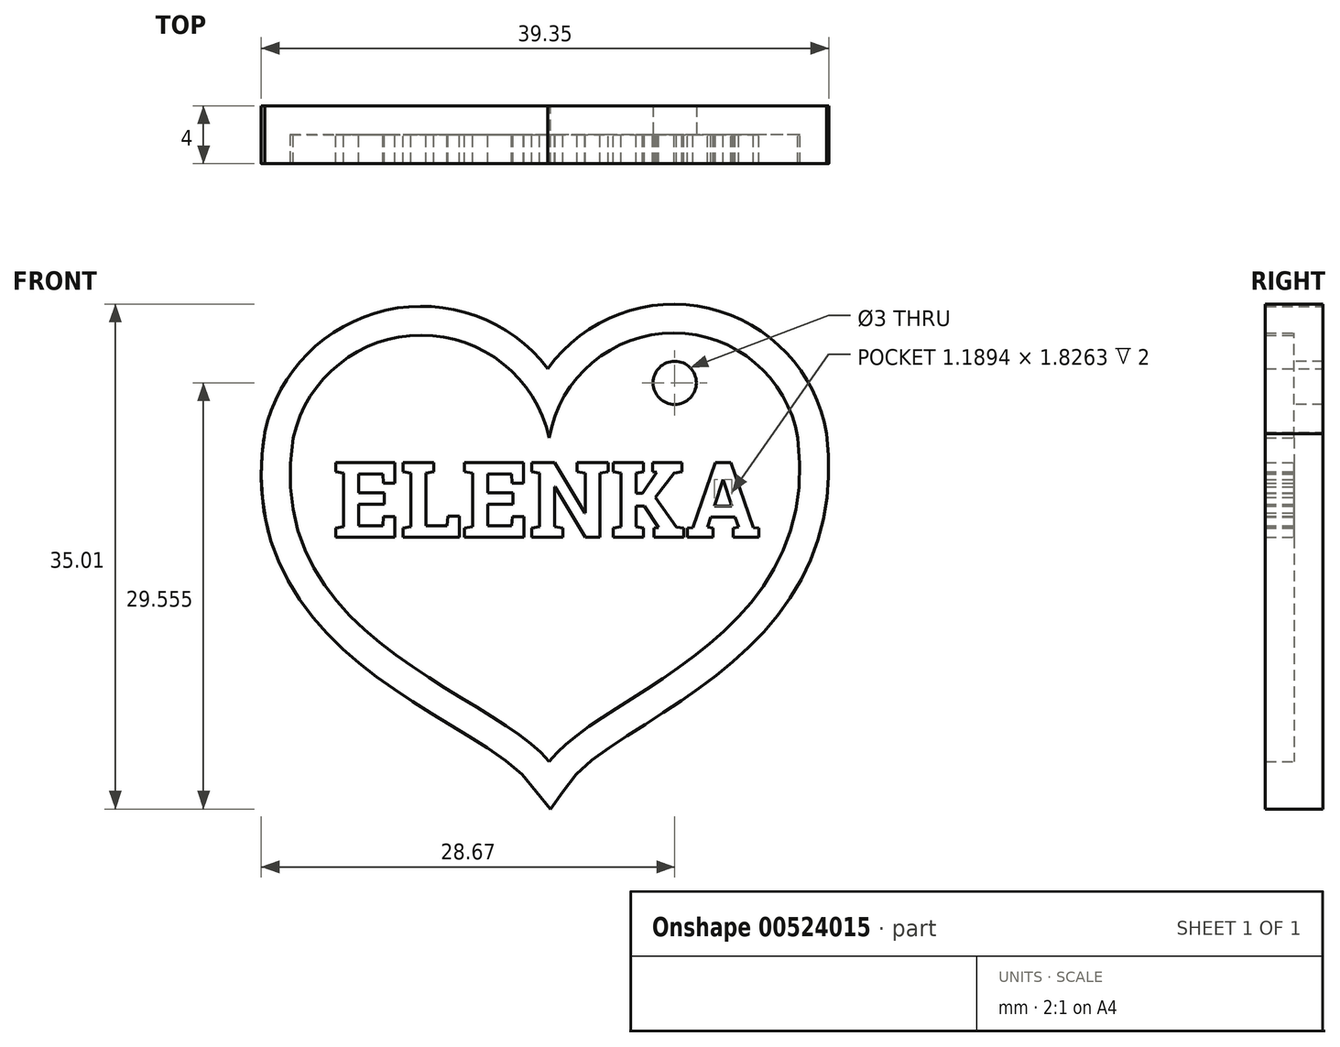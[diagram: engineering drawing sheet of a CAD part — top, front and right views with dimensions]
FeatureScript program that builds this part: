
annotation { "Feature Type Name" : "Feature", "Feature Type Description" : "" }
export const myFeature = defineFeature(function(context is Context, id is Id, definition is map)
    precondition{}
    {
        {
            var Q0;
            Q0=qCreatedBy(makeId("Front.planeOp"),FACE);
            var sketch = newSketch(context, id + "F0", { "sketchPlane" : qUnion([Q0])});
            skArc(sketch, "E0", {"start": v(17.25, 0) * mm, "mid": v(8.62, 7.26) * mm, "end": v(0, 0) * mm});
            skArc(sketch, "E1", {"start": v(0, 0) * mm, "mid": v(-8.88, 7.12) * mm, "end": v(-17.75, 0) * mm});
            skFitSpline(sketch, "E2", {"points": [v(-17.75, 0) * mm, v(0, -22.47) * mm], "startDerivative": vector(-6.74, -42.05) * mm, "endDerivative": vector(11.85, -14.75) * mm});
            skFitSpline(sketch, "E3", {"points": [v(17.25, 0) * mm, v(0, -22.47) * mm], "startDerivative": vector(5.09, -42.28) * mm, "endDerivative": vector(-10.5, -14.29) * mm});
            skSolve(sketch);
        }
        {
            var Q0;
            Q0=makeQuery(id+"F0.imprint","IMPRINT",FACE,{"disambiguationData":[TD([[makeQuery(id+"F0.imprint","IMPRINT",EDGE,{"derivedFrom":sQuery(id+"F0.wireOp",EDGE,"E0")}),1.0]])]});
            extrude(context, id + "F1", {"entities" : qUnion([Q0]), "depth" : 2 * mm, "offsetDistance" : 25 * mm});
        }
        {
            var Q0;
            Q0=makeQuery(id+"F1.opExtrude","CAP_FACE",FACE,{"disambiguationData":[OSD([sQuery(id+"F0.wireOp",EDGE,"E0"),sQuery(id+"F0.wireOp",EDGE,"E1"),sQuery(id+"F0.wireOp",EDGE,"E2"),sQuery(id+"F0.wireOp",EDGE,"E3")])],"isStart":false});
            shell(context, id + "F2", {"entities" : qUnion([Q0]), "thickness" : 2 * mm, "oppositeDirection" : true});
        }
        {
            var Q0;
            Q0=qCreatedBy(makeId("Front.planeOp"),FACE);
            var sketch = newSketch(context, id + "F3", { "sketchPlane" : qUnion([Q0])});
            skText(sketch, "E4", { "text": "ELENKA\n", "fontName": "RobotoSlab-Bold.ttf"});
            const initialGuessF3  = {"E4": [-0.015, -0.0069, 1, 0, 0.00525]};
            skSetInitialGuess(sketch, initialGuessF3);
            skSolve(sketch);
        }
        {
            var Q0;
            Q0 = qSketchRegion(id + "F3", true);
            extrude(context, id + "F4", {"entities" : qUnion([Q0]), "operationType" : NewBodyOperationType.ADD, "depth" : 2 * mm, "offsetDistance" : 25 * mm});
        }
        {
            var Q0;
            Q0=qCreatedBy(makeId("Front.planeOp"),FACE);
            var sketch = newSketch(context, id + "F5", { "sketchPlane" : qUnion([Q0])});
            skLineSegment(sketch, "E5", {"start": v(8.7, -24.79) * mm, "end": v(8.7, 3.8) * mm});
            skSolve(sketch);
        }
        {
            var Q0;
            Q0=sQuery(id+"F5.wireOp",VERTEX,"E5.end");
            var Q1;
            Q1=makeQuery(id+"F1.opExtrude","SWEPT_BODY",BODY,{"disambiguationData":[OSD([sQuery(id+"F0.wireOp",EDGE,"E0"),sQuery(id+"F0.wireOp",EDGE,"E1"),sQuery(id+"F0.wireOp",EDGE,"E2"),sQuery(id+"F0.wireOp",EDGE,"E3")])]});
            hole(context, id + "F6", {"style" : HoleStyle.SIMPLE, "endStyle" : HoleEndStyle.THROUGH, "holeDiameter" : 3 * mm, "isTappedThrough" : true, "tappedDepth" : 12 * mm, "tapClearance" : 3, "locations" : qUnion([Q0]), "scope" : qUnion([Q1])});
        }
    });
